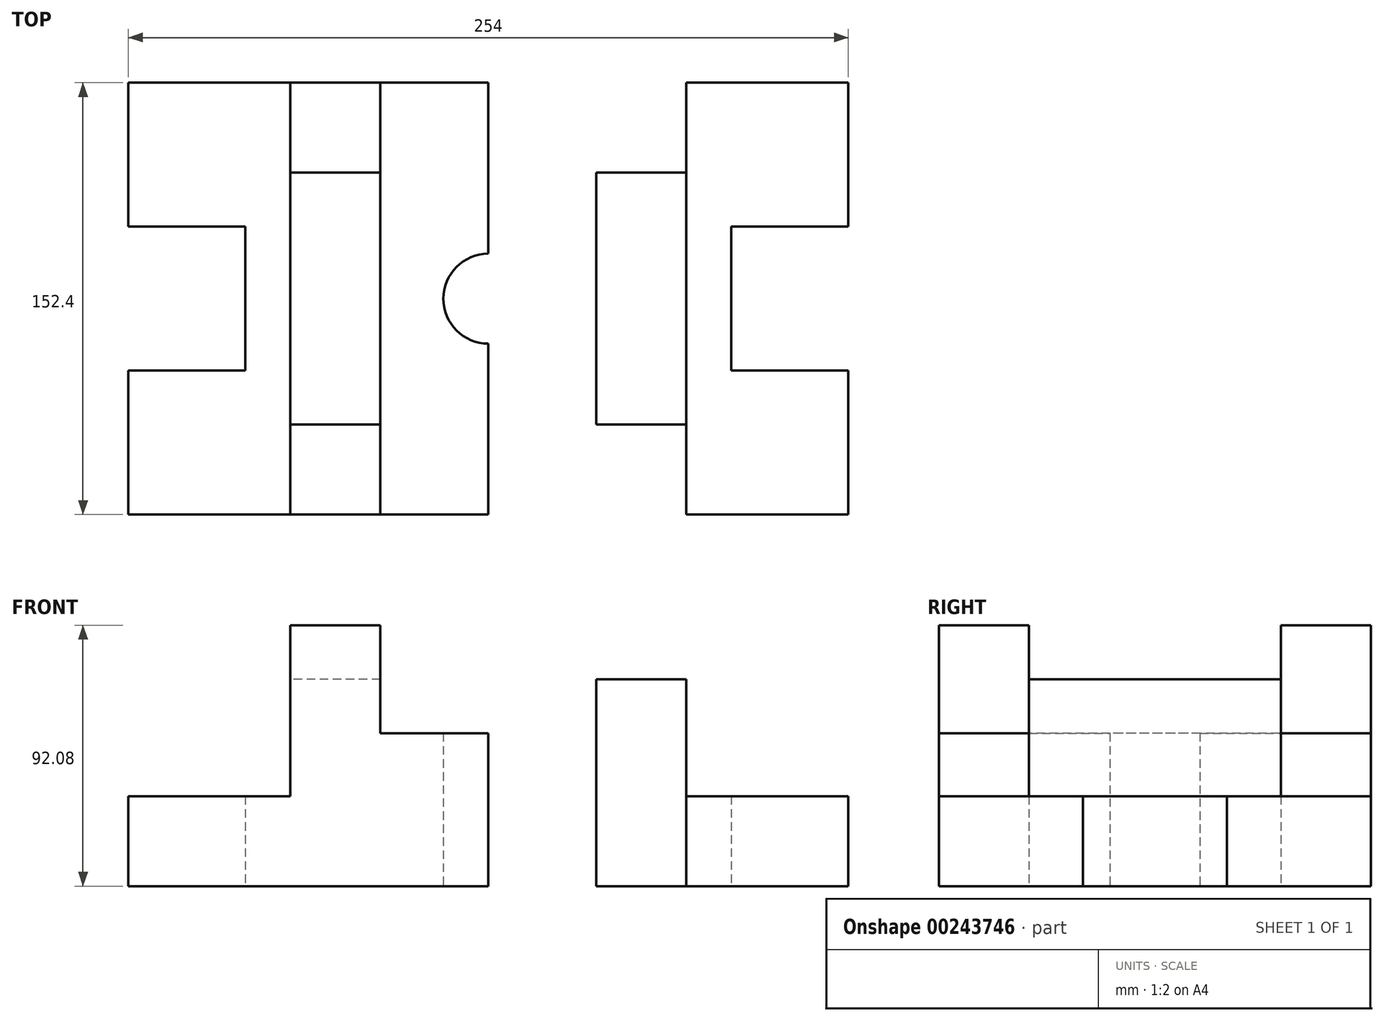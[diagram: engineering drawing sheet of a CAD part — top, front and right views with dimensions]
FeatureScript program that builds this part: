
annotation { "Feature Type Name" : "Feature", "Feature Type Description" : "" }
export const myFeature = defineFeature(function(context is Context, id is Id, definition is map)
    precondition{}
    {
        {
            var Q0;
            Q0=qCreatedBy(makeId("Top.planeOp"),FACE);
            var sketch = newSketch(context, id + "F0", { "sketchPlane" : qUnion([Q0])});
            skLineSegment(sketch, "E0", {"start": v(138.67, -69.95) * mm, "end": v(138.67, -19.15) * mm});
            skLineSegment(sketch, "E1", {"start": v(138.67, -19.15) * mm, "end": v(97.4, -19.15) * mm});
            skLineSegment(sketch, "E2", {"start": v(97.4, -19.15) * mm, "end": v(97.4, 31.65) * mm});
            skLineSegment(sketch, "E3", {"start": v(138.67, -69.95) * mm, "end": v(11.67, -69.95) * mm});
            skLineSegment(sketch, "E4", {"start": v(97.4, 31.65) * mm, "end": v(138.67, 31.65) * mm});
            skLineSegment(sketch, "E5", {"start": v(138.67, 31.65) * mm, "end": v(138.67, 82.45) * mm});
            skLineSegment(sketch, "E6", {"start": v(138.67, 82.45) * mm, "end": v(11.67, 82.45) * mm});
            skLineSegment(sketch, "E7", {"start": v(138.67, 82.45) * mm, "end": v(81.52, 82.45) * mm});
            skLineSegment(sketch, "E8", {"start": v(138.67, -69.95) * mm, "end": v(81.52, -69.95) * mm});
            skLineSegment(sketch, "E9", {"start": v(81.52, 82.45) * mm, "end": v(49.77, 82.45) * mm});
            skLineSegment(sketch, "E10", {"start": v(81.52, -69.95) * mm, "end": v(49.77, -69.95) * mm});
            skLineSegment(sketch, "E11", {"start": v(49.77, 82.45) * mm, "end": v(11.67, 82.45) * mm});
            skLineSegment(sketch, "E12", {"start": v(49.77, -69.95) * mm, "end": v(11.67, -69.95) * mm});
            skLineSegment(sketch, "E13", {"start": v(11.67, -69.95) * mm, "end": v(11.67, 82.45) * mm});
            skLineSegment(sketch, "E14", {"start": v(49.77, 82.45) * mm, "end": v(49.77, 50.7) * mm});
            skLineSegment(sketch, "E15", {"start": v(49.77, 50.7) * mm, "end": v(81.52, 50.7) * mm});
            skLineSegment(sketch, "E16", {"start": v(49.77, -69.95) * mm, "end": v(49.77, -38.2) * mm});
            skLineSegment(sketch, "E17", {"start": v(49.77, -38.2) * mm, "end": v(81.52, -38.2) * mm});
            skLineSegment(sketch, "E18.MirrorCS", {"start": v(-26.43, 82.45) * mm, "end": v(11.67, 82.45) * mm});
            skLineSegment(sketch, "E19.MirrorCS", {"start": v(-58.18, 82.45) * mm, "end": v(-26.43, 82.45) * mm});
            skLineSegment(sketch, "E20.MirrorCS", {"start": v(-26.43, 50.7) * mm, "end": v(-58.18, 50.7) * mm});
            skLineSegment(sketch, "E21.MirrorCS", {"start": v(-26.43, 82.45) * mm, "end": v(-26.43, 50.7) * mm});
            skLineSegment(sketch, "E22.MirrorCS", {"start": v(-115.33, 82.45) * mm, "end": v(-58.18, 82.45) * mm});
            skLineSegment(sketch, "E23.MirrorCS", {"start": v(-115.33, 31.65) * mm, "end": v(-115.33, 82.45) * mm});
            skLineSegment(sketch, "E24.MirrorCS", {"start": v(-74.05, 31.65) * mm, "end": v(-115.33, 31.65) * mm});
            skLineSegment(sketch, "E25.MirrorCS", {"start": v(-74.05, -19.15) * mm, "end": v(-74.05, 31.65) * mm});
            skLineSegment(sketch, "E26.MirrorCS", {"start": v(-115.33, -19.15) * mm, "end": v(-74.05, -19.15) * mm});
            skLineSegment(sketch, "E27.MirrorCS", {"start": v(-115.33, -69.95) * mm, "end": v(-115.33, -19.15) * mm});
            skLineSegment(sketch, "E28.MirrorCS", {"start": v(-115.33, -69.95) * mm, "end": v(-58.18, -69.95) * mm});
            skLineSegment(sketch, "E29.MirrorCS", {"start": v(-58.18, -69.95) * mm, "end": v(-26.43, -69.95) * mm});
            skLineSegment(sketch, "E30.MirrorCS", {"start": v(-26.43, -38.2) * mm, "end": v(-58.18, -38.2) * mm});
            skLineSegment(sketch, "E31.MirrorCS", {"start": v(-26.43, -69.95) * mm, "end": v(-26.43, -38.2) * mm});
            skLineSegment(sketch, "E32.MirrorCS", {"start": v(-115.33, -69.95) * mm, "end": v(11.67, -69.95) * mm});
            skLineSegment(sketch, "E33", {"start": v(81.52, 50.7) * mm, "end": v(81.52, 82.45) * mm});
            skLineSegment(sketch, "E34", {"start": v(81.52, -38.2) * mm, "end": v(81.52, -69.95) * mm});
            skLineSegment(sketch, "E35", {"start": v(81.52, -38.2) * mm, "end": v(81.52, 50.7) * mm});
            skLineSegment(sketch, "E36.MirrorCS", {"start": v(-58.18, 50.7) * mm, "end": v(-58.18, 82.45) * mm});
            skLineSegment(sketch, "E37.MirrorCS", {"start": v(-58.18, -38.2) * mm, "end": v(-58.18, 50.7) * mm});
            skLineSegment(sketch, "E38.MirrorCS", {"start": v(-58.18, -38.2) * mm, "end": v(-58.18, -69.95) * mm});
            skLineSegment(sketch, "E39", {"start": v(49.77, -38.2) * mm, "end": v(49.77, 50.7) * mm});
            skLineSegment(sketch, "E40.MirrorCS", {"start": v(-26.43, -38.2) * mm, "end": v(-26.43, 50.7) * mm});
            skCircle(sketch, "E41", {"center": v(11.67, 6.25) * mm, "radius": 15.88 * mm});
            skSolve(sketch);
        }
        {
            var Q0;
            Q0=makeQuery(id+"F0.imprint","IMPRINT",FACE,{"disambiguationData":[TD([[makeQuery(id+"F0.imprint","IMPRINT",EDGE,{"derivedFrom":sQuery(id+"F0.wireOp",EDGE,"E0")}),1.0]])]});
            var Q1;
            Q1=makeQuery(id+"F0.imprint","IMPRINT",FACE,{"disambiguationData":[TD([[makeQuery(id+"F0.imprint","IMPRINT",EDGE,{"derivedFrom":sQuery(id+"F0.wireOp",EDGE,"E9")}),1.0]])]});
            var Q2;
            Q2=makeQuery(id+"F0.imprint","IMPRINT",FACE,{"disambiguationData":[TD([[makeQuery(id+"F0.imprint","IMPRINT",EDGE,{"derivedFrom":sQuery(id+"F0.wireOp",EDGE,"E10")}),-1.0]])]});
            var Q3;
            Q3=makeQuery(id+"F0.imprint","IMPRINT",FACE,{"disambiguationData":[TD([[makeQuery(id+"F0.imprint","IMPRINT",EDGE,{"derivedFrom":sQuery(id+"F0.wireOp",EDGE,"E19.MirrorCS")}),-1.0]])]});
            var Q4;
            Q4=makeQuery(id+"F0.imprint","IMPRINT",FACE,{"disambiguationData":[TD([[makeQuery(id+"F0.imprint","IMPRINT",EDGE,{"derivedFrom":sQuery(id+"F0.wireOp",EDGE,"E22.MirrorCS")}),-1.0]])]});
            var Q5;
            Q5=makeQuery(id+"F0.imprint","IMPRINT",FACE,{"disambiguationData":[TD([[makeQuery(id+"F0.imprint","IMPRINT",EDGE,{"derivedFrom":sQuery(id+"F0.wireOp",EDGE,"E30.MirrorCS")}),1.0]])]});
            var Q6;
            {var subQ4=sQuery(id+"F0.wireOp",EDGE,"E18.MirrorCS");Q6=makeQuery(id+"F0.imprint","IMPRINT",FACE,{"disambiguationData":[TD([[makeQuery(id+"F0.imprint","IMPRINT",EDGE,{"derivedFrom":subQ4}),-1.0]])]});}
            var Q7;
            Q7=makeQuery(id+"F0.imprint","IMPRINT",FACE,{"disambiguationData":[TD([[makeQuery(id+"F0.imprint","IMPRINT",EDGE,{"derivedFrom":sQuery(id+"F0.wireOp",EDGE,"E20.MirrorCS")}),1.0]])]});
            var Q8;
            Q8=makeQuery(id+"F0.imprint","IMPRINT",FACE,{"disambiguationData":[TD([[makeQuery(id+"F0.imprint","IMPRINT",EDGE,{"derivedFrom":sQuery(id+"F0.wireOp",EDGE,"E15")}),-1.0]])]});
            var Q9;
            {var subQ1=sQuery(id+"F0.wireOp",EDGE,"E11");Q9=makeQuery(id+"F0.imprint","IMPRINT",FACE,{"disambiguationData":[TD([[makeQuery(id+"F0.imprint","IMPRINT",EDGE,{"derivedFrom":subQ1}),1.0]])]});}
            extrude(context, id + "F1", {"entities" : qUnion([Q0, Q1, Q2, Q3, Q4, Q5, Q6, Q7, Q8, Q9]), "depth" : 31.75 * mm});
        }
        {
            var Q0;
            Q0=makeQuery(id+"F0.imprint","IMPRINT",FACE,{"disambiguationData":[TD([[makeQuery(id+"F0.imprint","IMPRINT",EDGE,{"derivedFrom":sQuery(id+"F0.wireOp",EDGE,"E20.MirrorCS")}),1.0]])]});
            var Q1;
            Q1=makeQuery(id+"F0.imprint","IMPRINT",FACE,{"disambiguationData":[TD([[makeQuery(id+"F0.imprint","IMPRINT",EDGE,{"derivedFrom":sQuery(id+"F0.wireOp",EDGE,"E15")}),-1.0]])]});
            extrude(context, id + "F2", {"entities" : qUnion([Q0, Q1]), "operationType" : NewBodyOperationType.ADD, "depth" : 50.8 * mm});
        }
        {
            var Q0;
            Q0=makeQuery(id+"F0.imprint","IMPRINT",FACE,{"disambiguationData":[TD([[makeQuery(id+"F0.imprint","IMPRINT",EDGE,{"derivedFrom":sQuery(id+"F0.wireOp",EDGE,"E19.MirrorCS")}),-1.0]])]});
            var Q1;
            Q1=makeQuery(id+"F0.imprint","IMPRINT",FACE,{"disambiguationData":[TD([[makeQuery(id+"F0.imprint","IMPRINT",EDGE,{"derivedFrom":sQuery(id+"F0.wireOp",EDGE,"E30.MirrorCS")}),1.0]])]});
            var Q2;
            Q2=makeQuery(id+"F0.imprint","IMPRINT",FACE,{"disambiguationData":[TD([[makeQuery(id+"F0.imprint","IMPRINT",EDGE,{"derivedFrom":sQuery(id+"F0.wireOp",EDGE,"E10")}),-1.0]])]});
            var Q3;
            Q3=makeQuery(id+"F0.imprint","IMPRINT",FACE,{"disambiguationData":[TD([[makeQuery(id+"F0.imprint","IMPRINT",EDGE,{"derivedFrom":sQuery(id+"F0.wireOp",EDGE,"E9")}),1.0]])]});
            extrude(context, id + "F3", {"entities" : qUnion([Q0, Q1, Q2, Q3]), "operationType" : NewBodyOperationType.ADD, "depth" : 69.85 * mm});
        }
        {
            var Q0;
            {var subQ0=sQuery(id+"F0.wireOp",EDGE,"E19.MirrorCS");var subQ1=sQuery(id+"F0.wireOp",EDGE,"E9");var subQ2=sQuery(id+"F0.wireOp",EDGE,"E32.MirrorCS");var subQ3=sQuery(id+"F0.wireOp",EDGE,"E12");var subQ4=sQuery(id+"F0.wireOp",EDGE,"E10");var subQ5=sQuery(id+"F0.wireOp",EDGE,"E8");var subQ6=sQuery(id+"F0.wireOp",EDGE,"E22.MirrorCS");var subQ7=sQuery(id+"F0.wireOp",EDGE,"E18.MirrorCS");var subQ8=sQuery(id+"F0.wireOp",EDGE,"E11");var subQ9=sQuery(id+"F0.wireOp",EDGE,"E7");var subQ10=sQuery(id+"F0.wireOp",EDGE,"E41");Q0=makeQuery(id+"F3.boolean.opBoolean","SPLIT",FACE,{"disambiguationData":[TD([makeQuery(id+"F1.opExtrude","SWEPT_FACE",FACE,{"disambiguationData":[OSD([subQ10])]})])],"derivedFrom":makeQuery(id+"F1.opExtrude","CAP_FACE",FACE,{"disambiguationData":[OSD([sQuery(id+"F0.wireOp",EDGE,"E0"),sQuery(id+"F0.wireOp",EDGE,"E1"),sQuery(id+"F0.wireOp",EDGE,"E2"),sQuery(id+"F0.wireOp",EDGE,"E4"),sQuery(id+"F0.wireOp",EDGE,"E5"),subQ9,subQ5,subQ1,subQ4,subQ8,subQ3,subQ7,subQ0,subQ6,sQuery(id+"F0.wireOp",EDGE,"E23.MirrorCS"),sQuery(id+"F0.wireOp",EDGE,"E24.MirrorCS"),sQuery(id+"F0.wireOp",EDGE,"E25.MirrorCS"),sQuery(id+"F0.wireOp",EDGE,"E26.MirrorCS"),sQuery(id+"F0.wireOp",EDGE,"E27.MirrorCS"),subQ2,subQ10])],"isStart":false})});}
            extrude(context, id + "F4", {"entities" : qUnion([Q0]), "operationType" : NewBodyOperationType.ADD, "depth" : 19.05 * mm});
        }
        {
            var Q0;
            Q0=makeQuery(id+"F0.imprint","IMPRINT",FACE,{"disambiguationData":[TD([[makeQuery(id+"F0.imprint","IMPRINT",EDGE,{"derivedFrom":sQuery(id+"F0.wireOp",EDGE,"E19.MirrorCS")}),-1.0]])]});
            var Q1;
            Q1=makeQuery(id+"F0.imprint","IMPRINT",FACE,{"disambiguationData":[TD([[makeQuery(id+"F0.imprint","IMPRINT",EDGE,{"derivedFrom":sQuery(id+"F0.wireOp",EDGE,"E30.MirrorCS")}),1.0]])]});
            var Q2;
            Q2=makeQuery(id+"F0.imprint","IMPRINT",FACE,{"disambiguationData":[TD([[makeQuery(id+"F0.imprint","IMPRINT",EDGE,{"derivedFrom":sQuery(id+"F0.wireOp",EDGE,"E10")}),-1.0]])]});
            var Q3;
            Q3=makeQuery(id+"F0.imprint","IMPRINT",FACE,{"disambiguationData":[TD([[makeQuery(id+"F0.imprint","IMPRINT",EDGE,{"derivedFrom":sQuery(id+"F0.wireOp",EDGE,"E9")}),1.0]])]});
            extrude(context, id + "F5", {"entities" : qUnion([Q0, Q1, Q2, Q3]), "operationType" : NewBodyOperationType.ADD, "depth" : 92.07 * mm});
        }
        {
            var Q0;
            Q0=makeQuery(id+"F0.imprint","IMPRINT",FACE,{"disambiguationData":[TD([[makeQuery(id+"F0.imprint","IMPRINT",EDGE,{"derivedFrom":sQuery(id+"F0.wireOp",EDGE,"E15")}),-1.0]])]});
            var Q1;
            Q1=makeQuery(id+"F0.imprint","IMPRINT",FACE,{"disambiguationData":[TD([[makeQuery(id+"F0.imprint","IMPRINT",EDGE,{"derivedFrom":sQuery(id+"F0.wireOp",EDGE,"E20.MirrorCS")}),1.0]])]});
            extrude(context, id + "F6", {"entities" : qUnion([Q0, Q1]), "operationType" : NewBodyOperationType.ADD, "depth" : 73.02 * mm});
        }
        {
            var Q0;
            {var subQ4=sQuery(id+"F0.wireOp",EDGE,"E18.MirrorCS");Q0=makeQuery(id+"F0.imprint","IMPRINT",FACE,{"disambiguationData":[TD([[makeQuery(id+"F0.imprint","IMPRINT",EDGE,{"derivedFrom":subQ4}),-1.0]])]});}
            var Q1;
            {var subQ1=sQuery(id+"F0.wireOp",EDGE,"E11");Q1=makeQuery(id+"F0.imprint","IMPRINT",FACE,{"disambiguationData":[TD([[makeQuery(id+"F0.imprint","IMPRINT",EDGE,{"derivedFrom":subQ1}),1.0]])]});}
            extrude(context, id + "F7", {"entities" : qUnion([Q0, Q1]), "operationType" : NewBodyOperationType.ADD, "depth" : 53.97 * mm});
        }
    });
